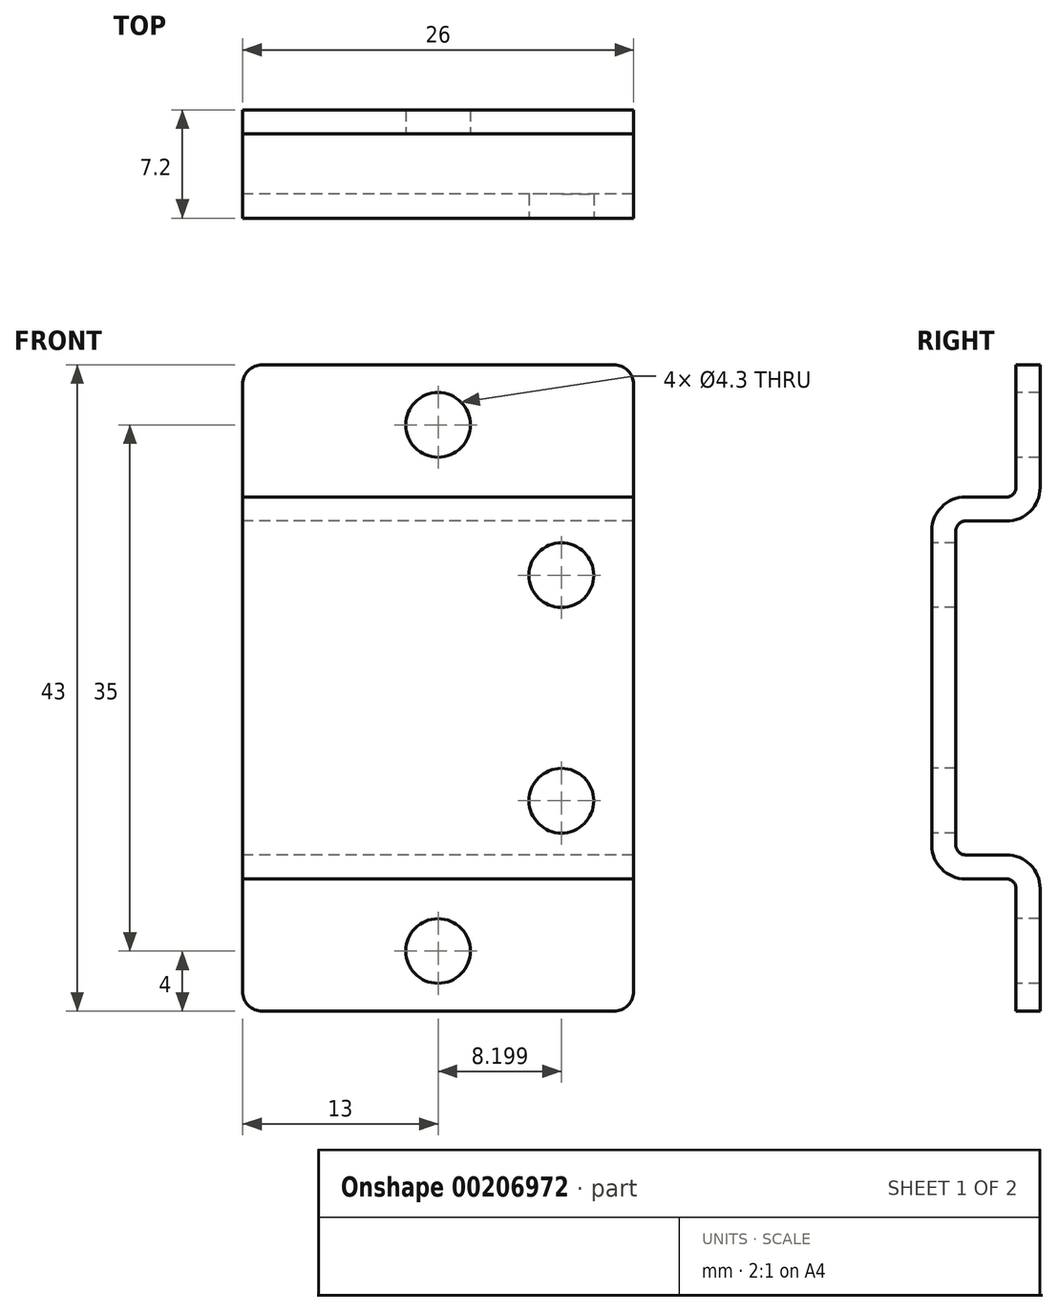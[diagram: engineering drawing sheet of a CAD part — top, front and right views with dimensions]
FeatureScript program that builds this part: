
annotation { "Feature Type Name" : "Feature", "Feature Type Description" : "" }
export const myFeature = defineFeature(function(context is Context, id is Id, definition is map)
    precondition{}
    {
        {
            var Q0;
            Q0=qCreatedBy(makeId("Right.planeOp"),FACE);
            var sketch = newSketch(context, id + "F0", { "sketchPlane" : qUnion([Q0])});
            skArc(sketch, "E0", {"start": v(-44.57, 3.67) * mm, "mid": v(-44.2, 2.77) * mm, "end": v(-43.3, 2.4) * mm});
            skLineSegment(sketch, "E1", {"start": v(-44.57, 10.56) * mm, "end": v(-44.57, 3.67) * mm});
            skLineSegment(sketch, "E2", {"start": v(-18.57, 10.56) * mm, "end": v(-18.57, 3.67) * mm});
            skArc(sketch, "E3", {"start": v(-19.84, 2.4) * mm, "mid": v(-18.95, 2.77) * mm, "end": v(-18.57, 3.67) * mm});
            skCircle(sketch, "E4", {"center": v(-31.57, 6.4) * mm, "radius": 2.15 * mm});
            skLineSegment(sketch, "E5", {"start": v(-19.84, 2.4) * mm, "end": v(-43.3, 2.4) * mm});
            skLineSegment(sketch, "E6", {"start": v(-44.57, 12.8) * mm, "end": v(-18.57, 12.8) * mm});
            skLineSegment(sketch, "E7", {"start": v(-44.57, 10.56) * mm, "end": v(-44.57, 12.8) * mm});
            skLineSegment(sketch, "E8", {"start": v(-18.57, 12.8) * mm, "end": v(-18.57, 10.56) * mm});
            skLineSegment(sketch, "E9", {"start": v(-18.57, 35) * mm, "end": v(-44.57, 35) * mm});
            skLineSegment(sketch, "E10", {"start": v(-44.57, 35) * mm, "end": v(-44.57, 37.23) * mm});
            skLineSegment(sketch, "E11", {"start": v(-18.57, 37.23) * mm, "end": v(-18.57, 35) * mm});
            skArc(sketch, "E12", {"start": v(-18.57, 44.13) * mm, "mid": v(-18.95, 45.03) * mm, "end": v(-19.84, 45.4) * mm});
            skArc(sketch, "E13", {"start": v(-43.3, 45.4) * mm, "mid": v(-44.2, 45.03) * mm, "end": v(-44.57, 44.13) * mm});
            skLineSegment(sketch, "E14", {"start": v(-19.84, 45.4) * mm, "end": v(-43.3, 45.4) * mm});
            skCircle(sketch, "E15", {"center": v(-31.57, 41.4) * mm, "radius": 2.15 * mm});
            skLineSegment(sketch, "E16", {"start": v(-44.57, 44.13) * mm, "end": v(-44.57, 37.23) * mm});
            skLineSegment(sketch, "E17", {"start": v(-18.57, 44.13) * mm, "end": v(-18.57, 37.23) * mm});
            skLineSegment(sketch, "E18", {"start": v(-44.57, 12.8) * mm, "end": v(-44.57, 13.43) * mm});
            skLineSegment(sketch, "E19", {"start": v(-18.57, 13.43) * mm, "end": v(-18.57, 12.8) * mm});
            skLineSegment(sketch, "E20", {"start": v(-44.57, 34.36) * mm, "end": v(-44.57, 35) * mm});
            skLineSegment(sketch, "E21", {"start": v(-18.57, 35) * mm, "end": v(-18.57, 34.36) * mm});
            skCircle(sketch, "E22", {"center": v(-39.77, 31.4) * mm, "radius": 2.15 * mm});
            skCircle(sketch, "E23", {"center": v(-39.77, 16.4) * mm, "radius": 2.15 * mm});
            skLineSegment(sketch, "E24", {"start": v(-44.57, 34.36) * mm, "end": v(-44.57, 13.43) * mm});
            skLineSegment(sketch, "E25", {"start": v(-18.57, 34.36) * mm, "end": v(-18.57, 13.43) * mm});
            skArc(sketch, "E26", {"start": v(-0.64, 32.6) * mm, "mid": v(0.95, 33.25) * mm, "end": v(1.6, 34.84) * mm});
            skLineSegment(sketch, "E27", {"start": v(-0.64, 32.6) * mm, "end": v(-3.37, 32.6) * mm});
            skArc(sketch, "E28", {"start": v(-3.37, 32.6) * mm, "mid": v(-3.81, 32.41) * mm, "end": v(-4, 31.97) * mm});
            skLineSegment(sketch, "E29", {"start": v(-4, 31.97) * mm, "end": v(-4, 11.04) * mm});
            skArc(sketch, "E30", {"start": v(-4, 11.04) * mm, "mid": v(-3.81, 10.59) * mm, "end": v(-3.37, 10.4) * mm});
            skLineSegment(sketch, "E31", {"start": v(-3.37, 10.4) * mm, "end": v(-0.64, 10.4) * mm});
            skArc(sketch, "E32", {"start": v(1.6, 8.16) * mm, "mid": v(0.95, 9.75) * mm, "end": v(-0.64, 10.4) * mm});
            skLineSegment(sketch, "E33", {"start": v(1.6, 8.16) * mm, "end": v(1.6, 1.27) * mm});
            skLineSegment(sketch, "E34", {"start": v(0, 1.27) * mm, "end": v(0, 8.17) * mm});
            skArc(sketch, "E35", {"start": v(0, 8.17) * mm, "mid": v(-0.19, 8.61) * mm, "end": v(-0.63, 8.8) * mm});
            skLineSegment(sketch, "E36", {"start": v(-0.63, 8.8) * mm, "end": v(-3.36, 8.8) * mm});
            skLineSegment(sketch, "E37", {"start": v(-3.36, 34.2) * mm, "end": v(-0.63, 34.2) * mm});
            skArc(sketch, "E38", {"start": v(-0.63, 34.2) * mm, "mid": v(-0.19, 34.39) * mm, "end": v(0, 34.84) * mm});
            skLineSegment(sketch, "E39", {"start": v(0, 34.84) * mm, "end": v(0, 41.73) * mm});
            skLineSegment(sketch, "E40", {"start": v(1.6, 41.73) * mm, "end": v(1.6, 34.84) * mm});
            skArc(sketch, "E41", {"start": v(-3.36, 34.2) * mm, "mid": v(-4.95, 33.55) * mm, "end": v(-5.6, 31.96) * mm});
            skArc(sketch, "E42", {"start": v(-5.6, 11.04) * mm, "mid": v(-4.95, 9.45) * mm, "end": v(-3.36, 8.8) * mm});
            skLineSegment(sketch, "E43", {"start": v(-5.6, 11.04) * mm, "end": v(-5.6, 31.96) * mm});
            skLineSegment(sketch, "E44", {"start": v(1.6, 0) * mm, "end": v(0, 0) * mm});
            skLineSegment(sketch, "E45", {"start": v(1.6, 1.27) * mm, "end": v(1.6, 0) * mm});
            skLineSegment(sketch, "E46", {"start": v(0, 0) * mm, "end": v(0, 1.27) * mm});
            skLineSegment(sketch, "E47", {"start": v(0, 43) * mm, "end": v(1.6, 43) * mm});
            skLineSegment(sketch, "E48", {"start": v(1.6, 43) * mm, "end": v(1.6, 41.73) * mm});
            skLineSegment(sketch, "E49", {"start": v(0, 41.73) * mm, "end": v(0, 43) * mm});
            skLineSegment(sketch, "E50", {"start": v(-28.4, 41.4) * mm, "end": v(-34.75, 41.4) * mm});
            skLineSegment(sketch, "E51", {"start": v(-31.57, 9.39) * mm, "end": v(-31.57, 44.39) * mm});
            skLineSegment(sketch, "E52", {"start": v(-36.6, 31.4) * mm, "end": v(-42.95, 31.4) * mm});
            skLineSegment(sketch, "E53", {"start": v(-39.77, 19.4) * mm, "end": v(-39.77, 34.38) * mm});
            skLineSegment(sketch, "E54", {"start": v(-36.6, 16.4) * mm, "end": v(-42.95, 16.4) * mm});
            skLineSegment(sketch, "E55", {"start": v(-39.77, 13.42) * mm, "end": v(-39.77, 19.4) * mm});
            skLineSegment(sketch, "E56", {"start": v(-28.4, 6.4) * mm, "end": v(-34.75, 6.4) * mm});
            skLineSegment(sketch, "E57", {"start": v(-31.57, 3.4) * mm, "end": v(-31.57, 9.39) * mm});
            skSolve(sketch);
        }
        {
            var Q0;
            Q0=makeQuery(id+"F0.imprint","IMPRINT",FACE,{"disambiguationData":[TD([[makeQuery(id+"F0.imprint","IMPRINT",EDGE,{"derivedFrom":sQuery(id+"F0.wireOp",EDGE,"E26")}),1.0]])]});
            extrude(context, id + "F1", {"entities" : qUnion([Q0]), "endBound" : BoundingType.SYMMETRIC, "depth" : 26 * mm});
        }
        {
            var Q0;
            Q0=makeQuery(id+"F1.opExtrude","SWEPT_FACE",FACE,{"disambiguationData":[OSD([sQuery(id+"F0.wireOp",EDGE,"E43")])]});
            var sketch = newSketch(context, id + "F2", { "sketchPlane" : qUnion([Q0])});
            skCircle(sketch, "E58", {"center": v(0, 4) * mm, "radius": 2.15 * mm});
            skCircle(sketch, "E59", {"center": v(0, 39) * mm, "radius": 2.15 * mm});
            skCircle(sketch, "E60", {"center": v(8.2, 29) * mm, "radius": 2.15 * mm});
            skCircle(sketch, "E61", {"center": v(8.2, 14) * mm, "radius": 2.15 * mm});
            skSolve(sketch);
        }
        {
            var Q0;
            Q0=qSketchRegion(id+"F2",true);
            extrude(context, id + "F3", {"entities" : qUnion([Q0]), "operationType" : NewBodyOperationType.REMOVE, "endBound" : BoundingType.THROUGH_ALL, "oppositeDirection" : true, "depth" : 25.4 * mm});
        }
        {
            var Q0;
            Q0=makeQuery(id+"F1.opExtrude","CAP_EDGE",EDGE,{"disambiguationData":[OSD([sQuery(id+"F0.wireOp",EDGE,"E47")])],"isStart":true});
            var Q1;
            Q1=makeQuery(id+"F1.opExtrude","CAP_EDGE",EDGE,{"disambiguationData":[OSD([sQuery(id+"F0.wireOp",EDGE,"E44")])],"isStart":true});
            var Q2;
            Q2=makeQuery(id+"F1.opExtrude","CAP_EDGE",EDGE,{"disambiguationData":[OSD([sQuery(id+"F0.wireOp",EDGE,"E44")])],"isStart":false});
            var Q3;
            Q3=makeQuery(id+"F1.opExtrude","CAP_EDGE",EDGE,{"disambiguationData":[OSD([sQuery(id+"F0.wireOp",EDGE,"E47")])],"isStart":false});
            fillet(context, id + "F4", {"entities" : qUnion([Q0, Q1, Q2, Q3]), "radius" : 1.3 * mm, "tangentPropagation" : true, "allowEdgeOverflow" : false});
        }
    });
